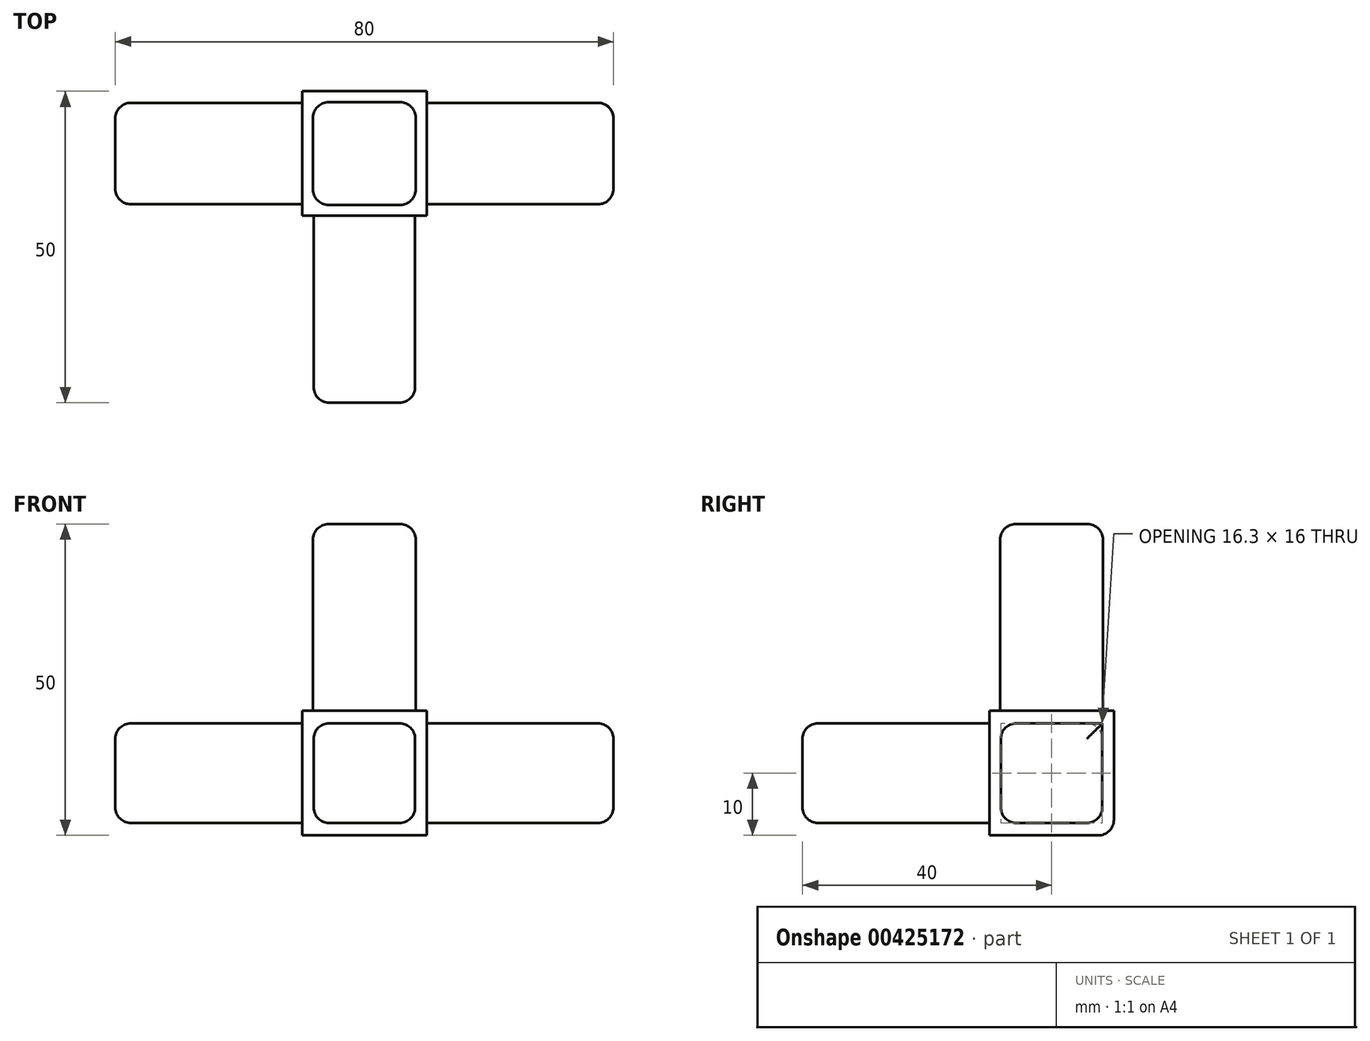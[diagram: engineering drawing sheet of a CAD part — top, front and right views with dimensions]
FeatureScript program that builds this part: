
annotation { "Feature Type Name" : "Feature", "Feature Type Description" : "" }
export const myFeature = defineFeature(function(context is Context, id is Id, definition is map)
    precondition{}
    {
        {
            var Q0;
            Q0=qCreatedBy(makeId("Front.planeOp"),FACE);
            var sketch = newSketch(context, id + "F0", { "sketchPlane" : qUnion([Q0])});
            skLineSegment(sketch, "E0.bottom", {"start": v(-10, -10) * mm, "end": v(10, -10) * mm});
            skLineSegment(sketch, "E0.top", {"start": v(-10, 10) * mm, "end": v(10, 10) * mm});
            skLineSegment(sketch, "E0.left", {"start": v(-10, -10) * mm, "end": v(-10, 10) * mm});
            skLineSegment(sketch, "E0.right", {"start": v(10, -10) * mm, "end": v(10, 10) * mm});
            skPoint(sketch, "E0.middle", {"position": v(0, 0) * mm});
            skLineSegment(sketch, "E1.bottom", {"start": v(-8.15, -8) * mm, "end": v(8.15, -8) * mm});
            skLineSegment(sketch, "E1.top", {"start": v(-8.15, 8) * mm, "end": v(8.15, 8) * mm});
            skLineSegment(sketch, "E1.left", {"start": v(-8.15, -8) * mm, "end": v(-8.15, 8) * mm});
            skLineSegment(sketch, "E1.right", {"start": v(8.15, -8) * mm, "end": v(8.15, 8) * mm});
            skSolve(sketch);
        }
        {
            var Q0;
            Q0=makeQuery(id+"F0.imprint","IMPRINT",FACE,{"disambiguationData":[TD([[makeQuery(id+"F0.imprint","IMPRINT",EDGE,{"derivedFrom":sQuery(id+"F0.wireOp",EDGE,"E1.bottom")}),1.0]])]});
            extrude(context, id + "F1", {"entities" : qUnion([Q0]), "depth" : 50 * mm});
        }
        {
            var Q0;
            Q0=qSketchRegion(id+"F0",true);
            extrude(context, id + "F2", {"entities" : qUnion([Q0]), "operationType" : NewBodyOperationType.ADD, "depth" : 20 * mm});
        }
        {
            var Q0;
            Q0=qCreatedBy(makeId("Right.planeOp"),FACE);
            var sketch = newSketch(context, id + "F3", { "sketchPlane" : qUnion([Q0])});
            skLineSegment(sketch, "E2.bottom", {"start": v(-1.85, -8) * mm, "end": v(-18.15, -8) * mm});
            skLineSegment(sketch, "E2.top", {"start": v(-1.85, 8) * mm, "end": v(-18.15, 8) * mm});
            skLineSegment(sketch, "E2.left", {"start": v(-1.85, -8) * mm, "end": v(-1.85, 8) * mm});
            skLineSegment(sketch, "E2.right", {"start": v(-18.15, -8) * mm, "end": v(-18.15, 8) * mm});
            skPoint(sketch, "E2.middle", {"position": v(-10, 0) * mm});
            skSolve(sketch);
        }
        {
            var Q0;
            Q0=qSketchRegion(id+"F3",true);
            extrude(context, id + "F4", {"entities" : qUnion([Q0]), "operationType" : NewBodyOperationType.ADD, "depth" : 40 * mm});
        }
        {
            var Q0;
            Q0=qCreatedBy(makeId("Right.planeOp"),FACE);
            var sketch = newSketch(context, id + "F5", { "sketchPlane" : qUnion([Q0])});
            skLineSegment(sketch, "E3.bottom", {"start": v(-1.85, -8) * mm, "end": v(-18.15, -8) * mm});
            skLineSegment(sketch, "E3.top", {"start": v(-1.85, 8) * mm, "end": v(-18.15, 8) * mm});
            skLineSegment(sketch, "E3.left", {"start": v(-1.85, -8) * mm, "end": v(-1.85, 8) * mm});
            skLineSegment(sketch, "E3.right", {"start": v(-18.15, -8) * mm, "end": v(-18.15, 8) * mm});
            skPoint(sketch, "E3.middle", {"position": v(-10, 0) * mm});
            skSolve(sketch);
        }
        {
            var Q0;
            Q0=qSketchRegion(id+"F5",true);
            extrude(context, id + "F6", {"entities" : qUnion([Q0]), "operationType" : NewBodyOperationType.ADD, "oppositeDirection" : true, "depth" : 40 * mm});
        }
        {
            var Q0;
            Q0=qCreatedBy(makeId("Top.planeOp"),FACE);
            var sketch = newSketch(context, id + "F7", { "sketchPlane" : qUnion([Q0])});
            skLineSegment(sketch, "E4.bottom", {"start": v(-8.25, -18.25) * mm, "end": v(8.25, -18.25) * mm});
            skLineSegment(sketch, "E4.top", {"start": v(-8.25, -1.75) * mm, "end": v(8.25, -1.75) * mm});
            skLineSegment(sketch, "E4.left", {"start": v(-8.25, -18.25) * mm, "end": v(-8.25, -1.75) * mm});
            skLineSegment(sketch, "E4.right", {"start": v(8.25, -18.25) * mm, "end": v(8.25, -1.75) * mm});
            skPoint(sketch, "E4.middle", {"position": v(0, -10) * mm});
            skSolve(sketch);
        }
        {
            var Q0;
            Q0=qSketchRegion(id+"F7",true);
            extrude(context, id + "F8", {"entities" : qUnion([Q0]), "operationType" : NewBodyOperationType.ADD, "depth" : 40 * mm});
        }
        {
            var Q0;
            Q0=makeQuery(id+"F2.opExtrude","CAP_EDGE",EDGE,{"disambiguationData":[OSD([sQuery(id+"F0.wireOp",EDGE,"E0.bottom")])],"isStart":true});
            var Q1;
            Q1=makeQuery(id+"F6.opExtrude","SWEPT_EDGE",EDGE,{"disambiguationData":[OSD([sQuery(id+"F5.wireOp",EDGE,"E3.bottom"),sQuery(id+"F5.wireOp",EDGE,"E3.left")])]});
            var Q2;
            Q2=makeQuery(id+"F6.opExtrude","SWEPT_EDGE",EDGE,{"disambiguationData":[OSD([sQuery(id+"F5.wireOp",EDGE,"E3.bottom"),sQuery(id+"F5.wireOp",EDGE,"E3.right")])]});
            var Q3;
            Q3=makeQuery(id+"F6.opExtrude","SWEPT_EDGE",EDGE,{"disambiguationData":[OSD([sQuery(id+"F5.wireOp",EDGE,"E3.top"),sQuery(id+"F5.wireOp",EDGE,"E3.left")])]});
            var Q4;
            Q4=makeQuery(id+"F6.opExtrude","SWEPT_EDGE",EDGE,{"disambiguationData":[OSD([sQuery(id+"F5.wireOp",EDGE,"E3.top"),sQuery(id+"F5.wireOp",EDGE,"E3.right")])]});
            var Q5;
            Q5=makeQuery(id+"F6.opExtrude","CAP_FACE",FACE,{"disambiguationData":[OSD([sQuery(id+"F5.wireOp",EDGE,"E3.bottom"),sQuery(id+"F5.wireOp",EDGE,"E3.top"),sQuery(id+"F5.wireOp",EDGE,"E3.left"),sQuery(id+"F5.wireOp",EDGE,"E3.right")])],"isStart":false});
            var Q6;
            Q6=makeQuery(id+"F8.opExtrude","SWEPT_EDGE",EDGE,{"disambiguationData":[OSD([sQuery(id+"F7.wireOp",EDGE,"E4.bottom"),sQuery(id+"F7.wireOp",EDGE,"E4.left")])]});
            var Q7;
            Q7=makeQuery(id+"F8.opExtrude","CAP_EDGE",EDGE,{"disambiguationData":[OSD([sQuery(id+"F7.wireOp",EDGE,"E4.bottom")])],"isStart":false});
            var Q8;
            Q8=makeQuery(id+"F8.opExtrude","CAP_FACE",FACE,{"disambiguationData":[OSD([sQuery(id+"F7.wireOp",EDGE,"E4.bottom"),sQuery(id+"F7.wireOp",EDGE,"E4.top"),sQuery(id+"F7.wireOp",EDGE,"E4.left"),sQuery(id+"F7.wireOp",EDGE,"E4.right")])],"isStart":false});
            var Q9;
            Q9=makeQuery(id+"F8.opExtrude","SWEPT_EDGE",EDGE,{"disambiguationData":[OSD([sQuery(id+"F7.wireOp",EDGE,"E4.top"),sQuery(id+"F7.wireOp",EDGE,"E4.left")])]});
            var Q10;
            Q10=makeQuery(id+"F8.opExtrude","SWEPT_EDGE",EDGE,{"disambiguationData":[OSD([sQuery(id+"F7.wireOp",EDGE,"E4.top"),sQuery(id+"F7.wireOp",EDGE,"E4.right")])]});
            var Q11;
            Q11=makeQuery(id+"F8.opExtrude","SWEPT_EDGE",EDGE,{"disambiguationData":[OSD([sQuery(id+"F7.wireOp",EDGE,"E4.bottom"),sQuery(id+"F7.wireOp",EDGE,"E4.right")])]});
            var Q12;
            Q12=makeQuery(id+"F1.opExtrude","SWEPT_EDGE",EDGE,{"disambiguationData":[OSD([sQuery(id+"F0.wireOp",EDGE,"E1.top"),sQuery(id+"F0.wireOp",EDGE,"E1.left")])]});
            var Q13;
            Q13=makeQuery(id+"F1.opExtrude","CAP_EDGE",EDGE,{"disambiguationData":[OSD([sQuery(id+"F0.wireOp",EDGE,"E1.top")])],"isStart":false});
            var Q14;
            Q14=makeQuery(id+"F1.opExtrude","SWEPT_EDGE",EDGE,{"disambiguationData":[OSD([sQuery(id+"F0.wireOp",EDGE,"E1.top"),sQuery(id+"F0.wireOp",EDGE,"E1.right")])]});
            var Q15;
            Q15=makeQuery(id+"F1.opExtrude","CAP_FACE",FACE,{"disambiguationData":[OSD([sQuery(id+"F0.wireOp",EDGE,"E1.bottom"),sQuery(id+"F0.wireOp",EDGE,"E1.top"),sQuery(id+"F0.wireOp",EDGE,"E1.left"),sQuery(id+"F0.wireOp",EDGE,"E1.right")])],"isStart":false});
            var Q16;
            Q16=makeQuery(id+"F4.opExtrude","SWEPT_EDGE",EDGE,{"disambiguationData":[OSD([sQuery(id+"F3.wireOp",EDGE,"E2.top"),sQuery(id+"F3.wireOp",EDGE,"E2.right")])]});
            var Q17;
            Q17=makeQuery(id+"F4.opExtrude","SWEPT_EDGE",EDGE,{"disambiguationData":[OSD([sQuery(id+"F3.wireOp",EDGE,"E2.bottom"),sQuery(id+"F3.wireOp",EDGE,"E2.right")])]});
            var Q18;
            Q18=makeQuery(id+"F4.opExtrude","CAP_FACE",FACE,{"disambiguationData":[OSD([sQuery(id+"F3.wireOp",EDGE,"E2.bottom"),sQuery(id+"F3.wireOp",EDGE,"E2.top"),sQuery(id+"F3.wireOp",EDGE,"E2.left"),sQuery(id+"F3.wireOp",EDGE,"E2.right")])],"isStart":false});
            var Q19;
            Q19=makeQuery(id+"F1.opExtrude","SWEPT_EDGE",EDGE,{"disambiguationData":[OSD([sQuery(id+"F0.wireOp",EDGE,"E1.bottom"),sQuery(id+"F0.wireOp",EDGE,"E1.right")])]});
            var Q20;
            Q20=makeQuery(id+"F1.opExtrude","SWEPT_EDGE",EDGE,{"disambiguationData":[OSD([sQuery(id+"F0.wireOp",EDGE,"E1.bottom"),sQuery(id+"F0.wireOp",EDGE,"E1.left")])]});
            var Q21;
            Q21=makeQuery(id+"F4.opExtrude","SWEPT_EDGE",EDGE,{"disambiguationData":[OSD([sQuery(id+"F3.wireOp",EDGE,"E2.bottom"),sQuery(id+"F3.wireOp",EDGE,"E2.left")])]});
            fillet(context, id + "F9", {"entities" : qUnion([Q0, Q1, Q2, Q3, Q4, Q5, Q6, Q7, Q8, Q9, Q10, Q11, Q12, Q13, Q14, Q15, Q16, Q17, Q18, Q19, Q20, Q21]), "radius" : 2.5 * mm, "tangentPropagation" : true, "allowEdgeOverflow" : false});
        }
    });
